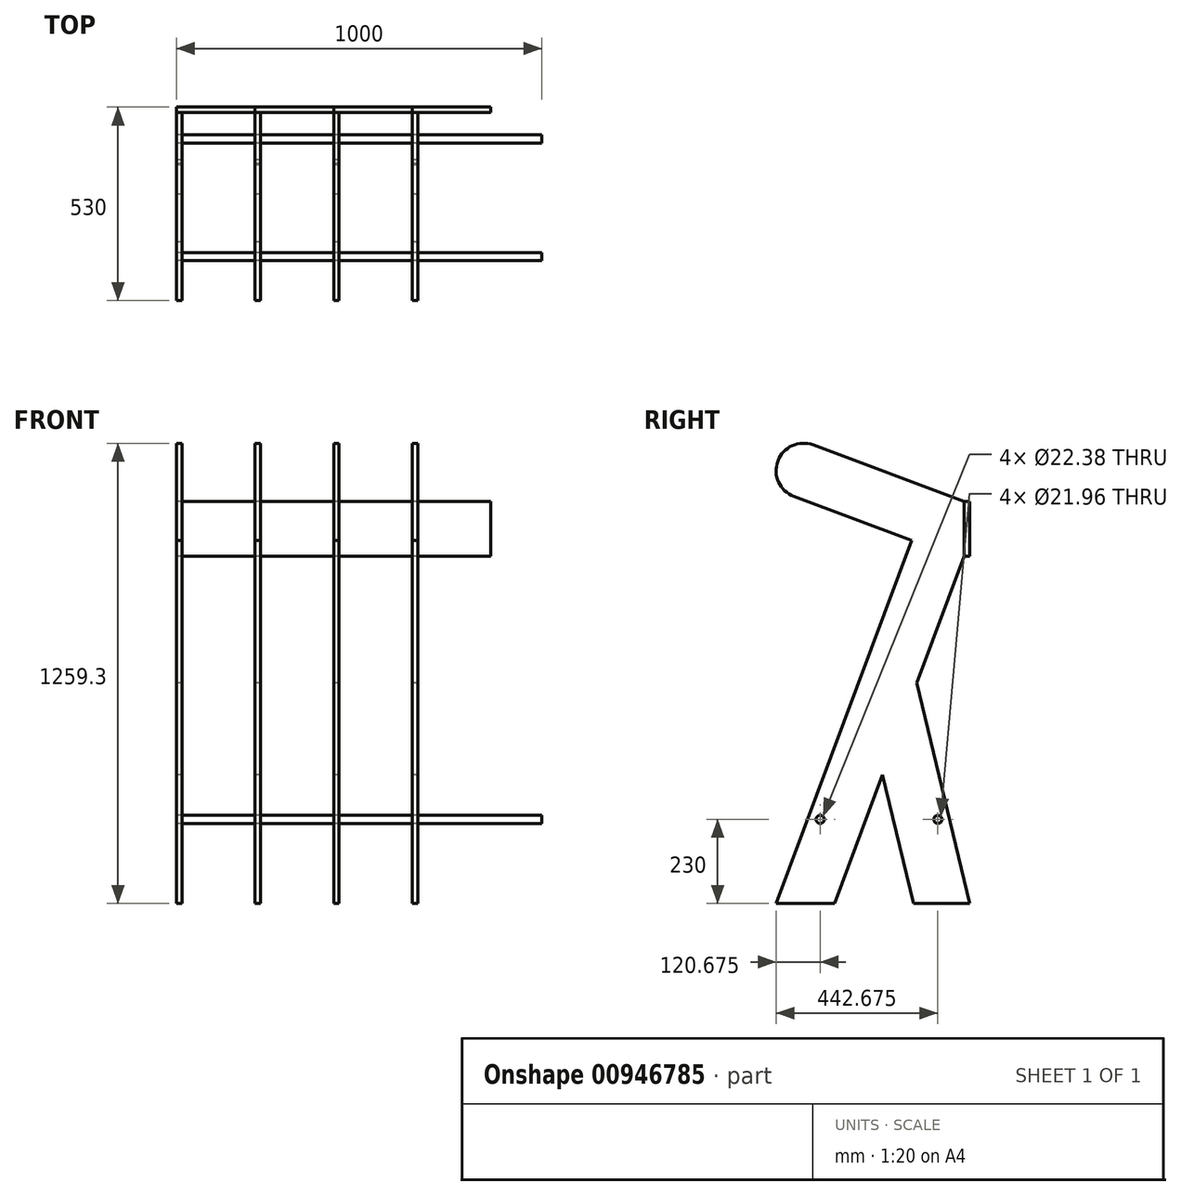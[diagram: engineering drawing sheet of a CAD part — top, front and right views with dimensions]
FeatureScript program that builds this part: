
annotation { "Feature Type Name" : "Feature", "Feature Type Description" : "" }
export const myFeature = defineFeature(function(context is Context, id is Id, definition is map)
    precondition{}
    {
        {
            var Q0;
            Q0=qCreatedBy(makeId("Right.planeOp"),FACE);
            var sketch = newSketch(context, id + "F0", { "sketchPlane" : qUnion([Q0])});
            skLineSegment(sketch, "E0", {"start": v(-481.25, 1114.04) * mm, "end": v(-158.83, 993.6) * mm});
            skLineSegment(sketch, "E1", {"start": v(-158.83, 993.6) * mm, "end": v(-530, 0) * mm});
            skLineSegment(sketch, "E2", {"start": v(-530, 0) * mm, "end": v(-369.88, 0) * mm});
            skLineSegment(sketch, "E3", {"start": v(0, 0) * mm, "end": v(-144.37, 603.67) * mm});
            skLineSegment(sketch, "E4", {"start": v(-144.37, 603.67) * mm, "end": v(-238.4, 351.95) * mm});
            skLineSegment(sketch, "E5", {"start": v(-238.4, 351.95) * mm, "end": v(-154.23, 0) * mm});
            skLineSegment(sketch, "E6", {"start": v(-154.23, 0) * mm, "end": v(0, 0) * mm});
            skLineSegment(sketch, "E7.bottom", {"start": v(0, 1100) * mm, "end": v(-15, 1100) * mm});
            skLineSegment(sketch, "E7.top", {"start": v(0, 950) * mm, "end": v(-15, 950) * mm});
            skLineSegment(sketch, "E7.left", {"start": v(0, 1100) * mm, "end": v(0, 950) * mm});
            skLineSegment(sketch, "E7.right", {"start": v(-15, 1100) * mm, "end": v(-15, 950) * mm});
            skLineSegment(sketch, "E8", {"start": v(-428.75, 1254.56) * mm, "end": v(-15, 1100) * mm});
            skLineSegment(sketch, "E9", {"start": v(-15, 950) * mm, "end": v(-369.88, 0) * mm});
            skCircle(sketch, "E10", {"center": v(-409.32, 230) * mm, "radius": 11.2 * mm});
            skCircle(sketch, "E11", {"center": v(-87.32, 230) * mm, "radius": 10.98 * mm});
            skLineSegment(sketch, "E12", {"start": v(-525.26, 1210.55) * mm, "end": v(-525.26, 1210.55) * mm});
            skLineSegment(sketch, "E13", {"start": v(-158.83, 993.6) * mm, "end": v(-18.32, 941.12) * mm});
            skArc(sketch, "E14.filletArc", {"start": v(-428.75, 1254.56) * mm, "mid": v(-486.12, 1252.54) * mm, "end": v(-525.26, 1210.55) * mm});
            skPoint(sketch, "E15.newPointA", {"position": v(-546.82, 1152.82) * mm});
            skPoint(sketch, "E15.newPointB", {"position": v(-585.05, 1152.82) * mm});
            skArc(sketch, "E15.filletArc", {"start": v(-525.26, 1210.55) * mm, "mid": v(-523.24, 1153.18) * mm, "end": v(-481.25, 1114.04) * mm});
            skSolve(sketch);
        }
        {
            var Q0;
            Q0=makeQuery(id+"F0.imprint","IMPRINT",FACE,{"disambiguationData":[TD([[makeQuery(id+"F0.imprint","IMPRINT",EDGE,{"derivedFrom":sQuery(id+"F0.wireOp",EDGE,"E0")}),1.0]])]});
            var Q1;
            Q1=makeQuery(id+"F0.imprint","IMPRINT",FACE,{"disambiguationData":[TD([[makeQuery(id+"F0.imprint","IMPRINT",EDGE,{"derivedFrom":sQuery(id+"F0.wireOp",EDGE,"E1")}),1.0]])]});
            var Q2;
            {var subQ2=sQuery(id+"F0.wireOp",EDGE,"E3");Q2=makeQuery(id+"F0.imprint","IMPRINT",FACE,{"disambiguationData":[TD([[makeQuery(id+"F0.imprint","IMPRINT",EDGE,{"derivedFrom":subQ2}),1.0]])]});}
            extrude(context, id + "F1", {"entities" : qUnion([Q0, Q1, Q2]), "depth" : 15 * mm, "offsetDistance" : 25 * mm});
        }
        {
            var Q0;
            Q0=makeQuery(id+"F0.imprint","IMPRINT",FACE,{"disambiguationData":[TD([[makeQuery(id+"F0.imprint","IMPRINT",EDGE,{"derivedFrom":sQuery(id+"F0.wireOp",EDGE,"E7.bottom")}),1.0]])]});
            extrude(context, id + "F2", {"entities" : qUnion([Q0]), "operationType" : NewBodyOperationType.ADD, "depth" : 215 * mm, "offsetDistance" : 25 * mm});
        }
        {
            var Q0;
            Q0=makeQuery(id+"F1.opExtrude","SWEPT_BODY",BODY,{"disambiguationData":[OSD([sQuery(id+"F0.wireOp",EDGE,"E0"),sQuery(id+"F0.wireOp",EDGE,"E1"),sQuery(id+"F0.wireOp",EDGE,"E2"),sQuery(id+"F0.wireOp",EDGE,"E3"),sQuery(id+"F0.wireOp",EDGE,"E5"),sQuery(id+"F0.wireOp",EDGE,"E6"),sQuery(id+"F0.wireOp",EDGE,"E7.right"),sQuery(id+"F0.wireOp",EDGE,"E8"),sQuery(id+"F0.wireOp",EDGE,"E9"),sQuery(id+"F0.wireOp",EDGE,"E10"),sQuery(id+"F0.wireOp",EDGE,"E11"),sQuery(id+"F0.wireOp",EDGE,"E14.filletArc"),sQuery(id+"F0.wireOp",EDGE,"E15.filletArc")])]});
            transform(context, id + "F3", {"entities" : qUnion([Q0]), "transformType" : TransformType.TRANSLATION_3D, "dx" : 215 * mm, "dy" : 0 * mm, "dz" : 0 * mm, "makeCopy" : true});
        }
        {
            var Q0;
            Q0=makeQuery(id+"F3.opPattern","COPY",BODY,{"derivedFrom":makeQuery(id+"F1.opExtrude","SWEPT_BODY",BODY,{"disambiguationData":[OSD([sQuery(id+"F0.wireOp",EDGE,"E0"),sQuery(id+"F0.wireOp",EDGE,"E1"),sQuery(id+"F0.wireOp",EDGE,"E2"),sQuery(id+"F0.wireOp",EDGE,"E3"),sQuery(id+"F0.wireOp",EDGE,"E5"),sQuery(id+"F0.wireOp",EDGE,"E6"),sQuery(id+"F0.wireOp",EDGE,"E7.right"),sQuery(id+"F0.wireOp",EDGE,"E8"),sQuery(id+"F0.wireOp",EDGE,"E9"),sQuery(id+"F0.wireOp",EDGE,"E10"),sQuery(id+"F0.wireOp",EDGE,"E11"),sQuery(id+"F0.wireOp",EDGE,"E14.filletArc"),sQuery(id+"F0.wireOp",EDGE,"E15.filletArc")])]}),"instanceName":"1"});
            transform(context, id + "F4", {"entities" : qUnion([Q0]), "transformType" : TransformType.TRANSLATION_3D, "dx" : 215 * mm, "dy" : 0 * mm, "dz" : 0 * mm, "makeCopy" : true});
        }
        {
            var Q0;
            Q0=makeQuery(id+"F4.opPattern","COPY",BODY,{"derivedFrom":makeQuery(id+"F3.opPattern","COPY",BODY,{"derivedFrom":makeQuery(id+"F1.opExtrude","SWEPT_BODY",BODY,{"disambiguationData":[OSD([sQuery(id+"F0.wireOp",EDGE,"E0"),sQuery(id+"F0.wireOp",EDGE,"E1"),sQuery(id+"F0.wireOp",EDGE,"E2"),sQuery(id+"F0.wireOp",EDGE,"E3"),sQuery(id+"F0.wireOp",EDGE,"E5"),sQuery(id+"F0.wireOp",EDGE,"E6"),sQuery(id+"F0.wireOp",EDGE,"E7.right"),sQuery(id+"F0.wireOp",EDGE,"E8"),sQuery(id+"F0.wireOp",EDGE,"E9"),sQuery(id+"F0.wireOp",EDGE,"E10"),sQuery(id+"F0.wireOp",EDGE,"E11"),sQuery(id+"F0.wireOp",EDGE,"E14.filletArc"),sQuery(id+"F0.wireOp",EDGE,"E15.filletArc")])]}),"instanceName":"1"}),"instanceName":"1"});
            transform(context, id + "F5", {"entities" : qUnion([Q0]), "transformType" : TransformType.TRANSLATION_3D, "dx" : 215 * mm, "dy" : 0 * mm, "dz" : 0 * mm, "makeCopy" : true});
        }
        {
            var Q0;
            Q0=qCreatedBy(makeId("Right.planeOp"),FACE);
            var sketch = newSketch(context, id + "F6", { "sketchPlane" : qUnion([Q0])});
            skCircle(sketch, "E16", {"center": v(-409.32, 230) * mm, "radius": 11.18 * mm});
            skSolve(sketch);
        }
        {
            var Q0;
            Q0 = qSketchRegion(id + "F6", true);
            extrude(context, id + "F7", {"entities" : qUnion([Q0]), "depth" : 1000 * mm, "offsetDistance" : 25 * mm});
        }
        {
            var Q0;
            Q0=qCreatedBy(makeId("Right.planeOp"),FACE);
            var sketch = newSketch(context, id + "F8", { "sketchPlane" : qUnion([Q0])});
            skCircle(sketch, "E17", {"center": v(-87.32, 230) * mm, "radius": 11 * mm});
            skSolve(sketch);
        }
        {
            var Q0;
            Q0 = qSketchRegion(id + "F8", true);
            extrude(context, id + "F9", {"entities" : qUnion([Q0]), "depth" : 1000 * mm, "offsetDistance" : 25 * mm});
        }
    });
